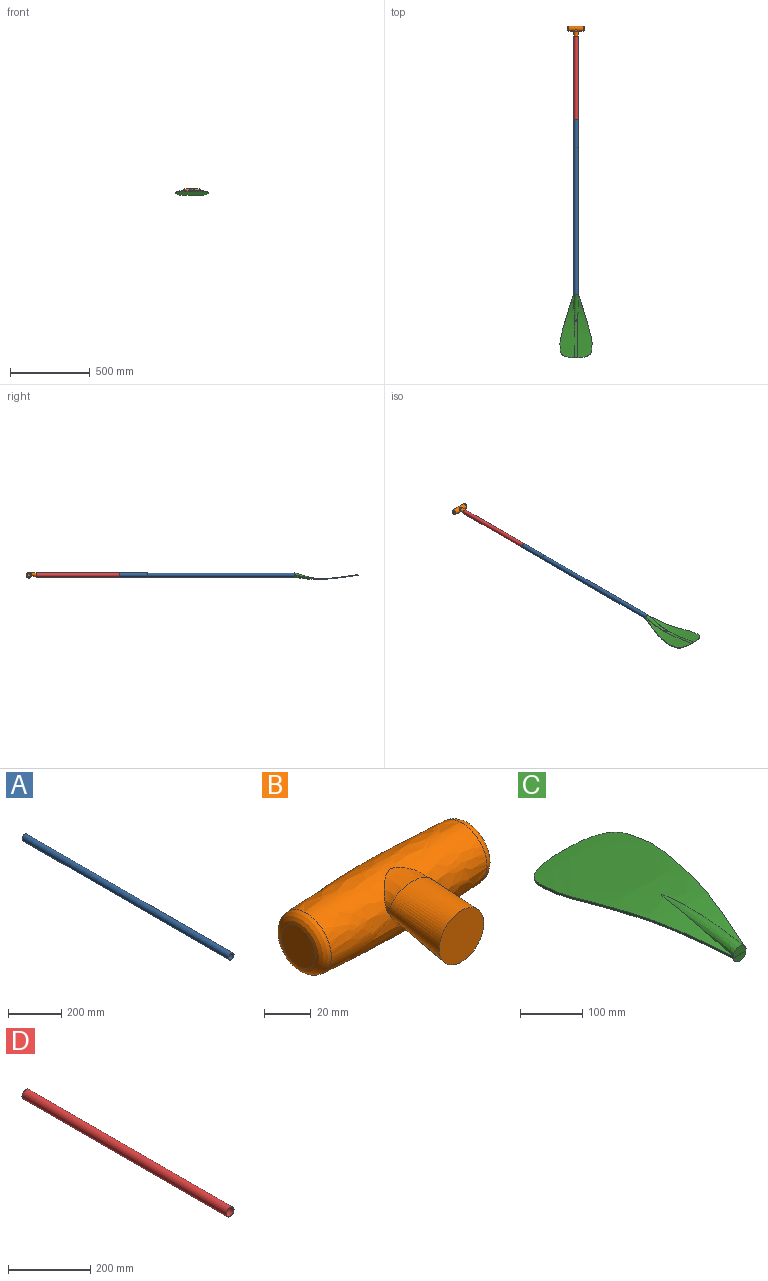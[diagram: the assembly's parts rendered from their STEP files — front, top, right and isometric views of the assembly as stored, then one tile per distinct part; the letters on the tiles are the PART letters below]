
ASSEMBLY  parts=4 mates=3
PART A: 4 faces, bbox 29x1100x29 mm
  f0: cylinder r=13.5mm len=1100mm, axis (0,1,0), area 93305.3mm2, adj f2,f3
  f1: cylinder r=14.5mm len=1100mm, axis (0,1,0), area 100216.8mm2, adj f2,f3
  f2: plane 29x29mm, normal (0,-1,0), area 88mm2, adj f0,f1
  f3: plane 29x29mm, normal (0,1,0), area 88mm2, adj f0,f1
PART B: 8 faces, bbox 104x64x34 mm
  f0: plane 27x27mm, normal (0,-1,0), area 572.5mm2, adj f1
  f1: bspline ~30x27.19mm, area 2366.1mm2, adj f0,f2
  f2: extruded ~27x18mm, area 301.4mm2, adj f1,f5
  f3: plane 20.56x20.56mm, normal (1,0,0), area 332mm2, adj f6
  f4: plane 20.56x20.56mm, normal (-1,0,0), area 332mm2, adj f7
  f5: bspline ~94.57x33.96mm, area 9248.2mm2, adj f2,f6,f7
  f6: bspline ~30.55x30.55mm, area 636.9mm2, adj f3,f5
  f7: bspline ~30.55x30.55mm, area 636.9mm2, adj f4,f5
PART C: 17 faces, bbox 204.5x403.8x65.8 mm
  f0: bspline ~400.79x99.76mm, area 1951.6mm2, adj f2,f6,f11,f12,f13
  f1: bspline ~400.79x99.77mm, area 1951.6mm2, adj f2,f5,f11,f12,f13
  f2: extruded ~400.31x201.44mm, area 51275mm2, adj f0,f1,f12,f13,f14
  f3: extruded ~0.48x0.16mm, area 0mm2, adj f9,f13,f16
  f4: plane 0.49x0.17mm, normal (0,0.24,-0.97), area 0.1mm2, adj f5,f10,f11,f13
  f5: plane 2.06x0.48mm, normal (1,0,0), area 0.5mm2, adj f1,f4,f13
  f6: plane 2.06x0.48mm, normal (-1,0,0), area 0.5mm2, adj f0,f7,f13
  f7: plane 0.49x0.17mm, normal (0,0.24,-0.97), area 0.1mm2, adj f6,f10,f11,f13
  f8: extruded ~0.48x0.16mm, area 0mm2, adj f9,f13,f16
  f9: plane 28.72x0.46mm, normal (0,0.24,-0.97), area 13.5mm2, adj f3,f8,f13,f16
  f10: bspline ~301.26x60.84mm, area 4388mm2, adj f4,f7,f11,f13,f15
  f11: extruded ~399.21x201.44mm, area 46593.8mm2, adj f0,f1,f4,f7,f10,f12,f15
  f12: plane 3.95x1.92mm, normal (0,0.99,-0.15), area 7.7mm2, adj f0,f1,f2,f11
  f13: plane 32.35x32.02mm, normal (0,-1,0), area 659.9mm2, adj f0,f1,f2,f3,f4,f5,f6,f7
  f14: bspline ~313.9x36.49mm, area 4390.1mm2, adj f2,f13
  f15: bspline ~349.84x65.6mm, area 5130.3mm2, adj f10,f11
  f16: bspline ~98.75x29.23mm, area 13.9mm2, adj f3,f8,f9,f13
PART D: 4 faces, bbox 27x700x27 mm
  f0: cylinder r=12.5mm len=700mm, axis (0,1,0), area 54977.9mm2, adj f2,f3
  f1: cylinder r=13.5mm len=700mm, axis (0,1,0), area 59376.1mm2, adj f2,f3
  f2: plane 27x27mm, normal (0,-1,0), area 81.7mm2, adj f0,f1
  f3: plane 27x27mm, normal (0,1,0), area 81.7mm2, adj f0,f1
PLACE A t=(0,-1070,0)mm
PLACE B at identity
PLACE C rot(axis=(1,0,0),180deg) t=(0,-1620,0)mm
PLACE D t=(0,-350,0)mm
MATE fastened C.f13 <-> A.f0  axis (0,1,0) through (0,-1620,0)mm
MATE fastened B.f0 <-> D.f1  axis (0,-1,0) through (0,0,0)mm
MATE slider D.f0 <-> A.f1  axis (0,1,0) through (0,-700,0)mm
